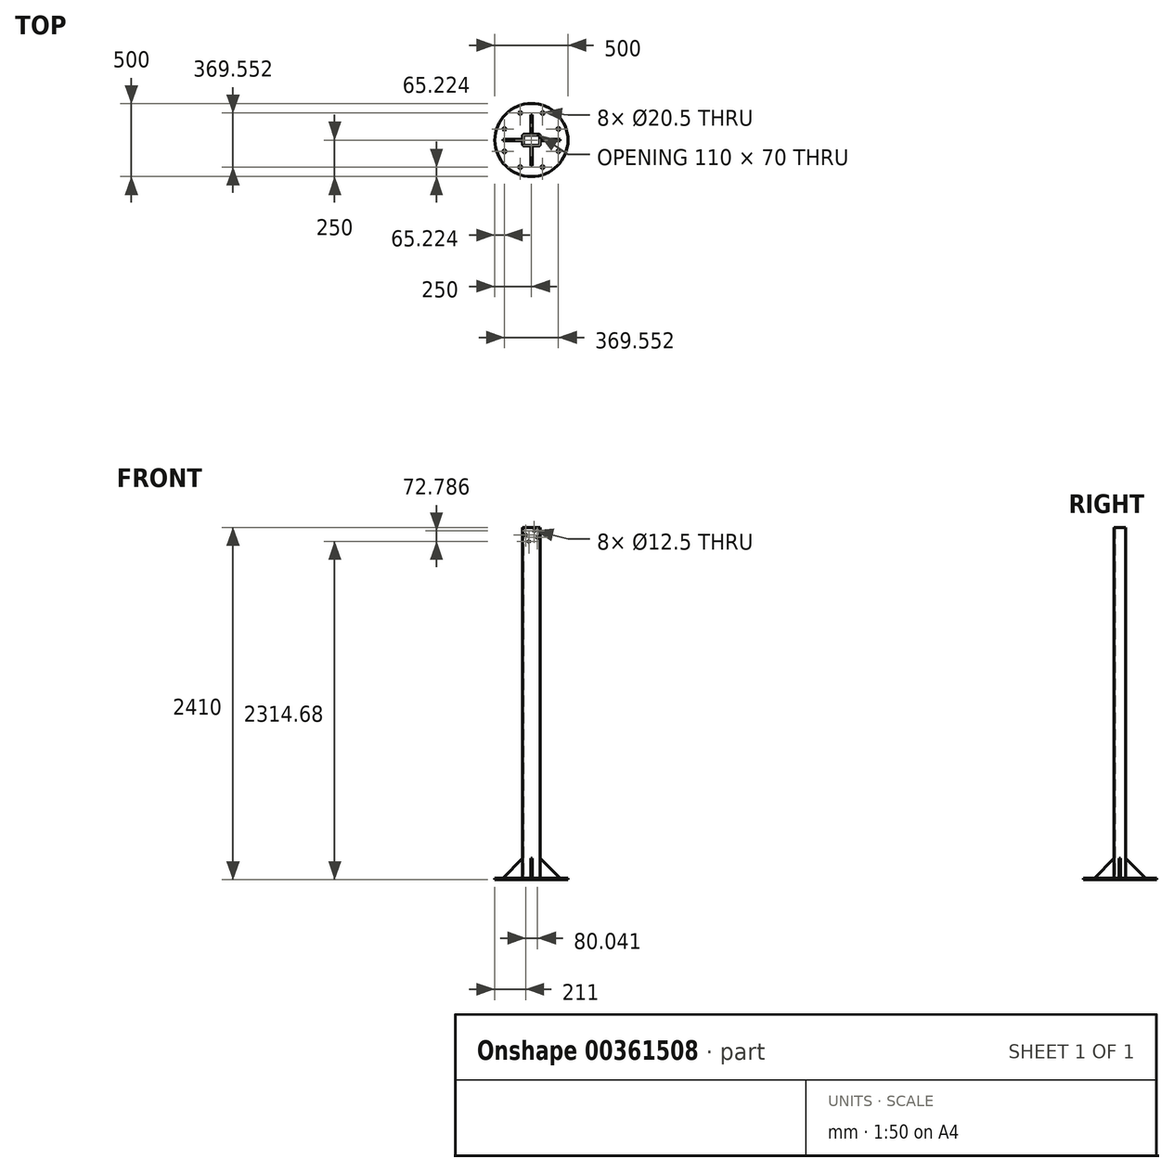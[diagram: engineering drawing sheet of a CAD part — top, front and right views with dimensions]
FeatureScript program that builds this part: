
annotation { "Feature Type Name" : "Feature", "Feature Type Description" : "" }
export const myFeature = defineFeature(function(context is Context, id is Id, definition is map)
    precondition{}
    {
        {
            var Q0;
            Q0=qCreatedBy(makeId("Top.planeOp"),FACE);
            var sketch = newSketch(context, id + "F0", { "sketchPlane" : qUnion([Q0])});
            skCircle(sketch, "E0", {"center": v(0, 0) * mm, "radius": 250 * mm});
            skCircle(sketch, "E1", {"center": v(76.54, 184.78) * mm, "radius": 10.25 * mm});
            skLineSegment(sketch, "E2", {"start": v(0, 0) * mm, "end": v(76.54, 184.78) * mm, "construction": true});
            skCircle(sketch, "E3.1.0", {"center": v(-76.54, 184.78) * mm, "radius": 10.25 * mm});
            skCircle(sketch, "E3.2.0", {"center": v(-184.78, 76.54) * mm, "radius": 10.25 * mm});
            skCircle(sketch, "E3.3.0", {"center": v(-184.78, -76.54) * mm, "radius": 10.25 * mm});
            skLineSegment(sketch, "E4", {"start": v(-76.54, 184.78) * mm, "end": v(0, 0) * mm, "construction": true});
            skCircle(sketch, "E5.1.4.0", {"center": v(-76.54, -184.78) * mm, "radius": 10.25 * mm});
            skCircle(sketch, "E5.1.5.0", {"center": v(76.54, -184.78) * mm, "radius": 10.25 * mm});
            skCircle(sketch, "E5.1.6.0", {"center": v(184.78, -76.54) * mm, "radius": 10.25 * mm});
            skCircle(sketch, "E5.1.7.0", {"center": v(184.78, 76.54) * mm, "radius": 10.25 * mm});
            skSolve(sketch);
        }
        {
            var Q0;
            Q0 = qSketchRegion(id + "F0", true);
            extrude(context, id + "F1", {"entities" : qUnion([Q0]), "depth" : 10 * mm});
        }
        {
            var Q0;
            Q0=makeQuery(id+"F1.opExtrude","CAP_FACE",FACE,{"disambiguationData":[OSD([sQuery(id+"F0.wireOp",EDGE,"E0")])],"isStart":false});
            var sketch = newSketch(context, id + "F2", { "sketchPlane" : qUnion([Q0])});
            skLineSegment(sketch, "E6.bottom", {"start": v(50, 40) * mm, "end": v(-50, 40) * mm});
            skLineSegment(sketch, "E6.top", {"start": v(50, -40) * mm, "end": v(-50, -40) * mm});
            skLineSegment(sketch, "E6.left", {"start": v(60, 30) * mm, "end": v(60, -30) * mm});
            skLineSegment(sketch, "E6.right", {"start": v(-60, 30) * mm, "end": v(-60, -30) * mm});
            skPoint(sketch, "E6.middle", {"position": v(0, 0) * mm});
            skPoint(sketch, "E7.visualSharp", {"position": v(60, 40) * mm});
            skArc(sketch, "E7.filletArc", {"start": v(60, 30) * mm, "mid": v(57.07, 37.07) * mm, "end": v(50, 40) * mm});
            skPoint(sketch, "E8.visualSharp", {"position": v(-60, 40) * mm});
            skArc(sketch, "E8.filletArc", {"start": v(-50, 40) * mm, "mid": v(-57.07, 37.07) * mm, "end": v(-60, 30) * mm});
            skPoint(sketch, "E9.visualSharp", {"position": v(-60, -40) * mm});
            skArc(sketch, "E9.filletArc", {"start": v(-60, -30) * mm, "mid": v(-57.07, -37.07) * mm, "end": v(-50, -40) * mm});
            skPoint(sketch, "E10.visualSharp", {"position": v(60, -40) * mm});
            skArc(sketch, "E10.filletArc", {"start": v(50, -40) * mm, "mid": v(57.07, -37.07) * mm, "end": v(60, -30) * mm});
            skArc(sketch, "E11.0", {"start": v(55, 30) * mm, "mid": v(53.54, 33.54) * mm, "end": v(50, 35) * mm});
            skLineSegment(sketch, "E11.1", {"start": v(55, 30) * mm, "end": v(55, -30) * mm});
            skLineSegment(sketch, "E11.2", {"start": v(50, 35) * mm, "end": v(-50, 35) * mm});
            skArc(sketch, "E11.3", {"start": v(50, -35) * mm, "mid": v(53.54, -33.54) * mm, "end": v(55, -30) * mm});
            skArc(sketch, "E11.4", {"start": v(-50, 35) * mm, "mid": v(-53.54, 33.54) * mm, "end": v(-55, 30) * mm});
            skLineSegment(sketch, "E11.5", {"start": v(-55, 30) * mm, "end": v(-55, -30) * mm});
            skArc(sketch, "E11.6", {"start": v(-55, -30) * mm, "mid": v(-53.54, -33.54) * mm, "end": v(-50, -35) * mm});
            skLineSegment(sketch, "E11.7", {"start": v(50, -35) * mm, "end": v(-50, -35) * mm});
            skSolve(sketch);
        }
        {
            var Q0;
            Q0 = qSketchRegion(id + "F2", true);
            extrude(context, id + "F3", {"entities" : qUnion([Q0]), "depth" : 2400 * mm});
        }
        {
            var Q0;
            Q0=qCreatedBy(makeId("Front.planeOp"),FACE);
            var sketch = newSketch(context, id + "F4", { "sketchPlane" : qUnion([Q0])});
            skLineSegment(sketch, "E12", {"start": v(-60, 145) * mm, "end": v(-195, 10) * mm});
            skLineSegment(sketch, "E13", {"start": v(-195, 10) * mm, "end": v(-60, 10) * mm});
            skLineSegment(sketch, "E14", {"start": v(-60, 10) * mm, "end": v(-60, 145) * mm});
            skSolve(sketch);
        }
        {
            var Q0;
            Q0 = qSketchRegion(id + "F4", true);
            extrude(context, id + "F5", {"entities" : qUnion([Q0]), "endBound" : BoundingType.SYMMETRIC, "depth" : 10 * mm});
        }
        {
            var Q0;
            Q0=qCreatedBy(makeId("Right.planeOp"),FACE);
            var sketch = newSketch(context, id + "F6", { "sketchPlane" : qUnion([Q0])});
            skLineSegment(sketch, "E15", {"start": v(-40, 10) * mm, "end": v(-40, 145) * mm});
            skLineSegment(sketch, "E16", {"start": v(-40, 145) * mm, "end": v(-175, 10) * mm});
            skLineSegment(sketch, "E17", {"start": v(-175, 10) * mm, "end": v(-40, 10) * mm});
            skSolve(sketch);
        }
        {
            var Q0;
            Q0 = qSketchRegion(id + "F6", true);
            extrude(context, id + "F7", {"entities" : qUnion([Q0]), "endBound" : BoundingType.SYMMETRIC, "depth" : 10 * mm});
        }
        {
            var Q0;
            Q0=makeQuery(id+"F7.opExtrude","SWEPT_BODY",BODY,{"disambiguationData":[OSD([sQuery(id+"F6.wireOp",EDGE,"E15"),sQuery(id+"F6.wireOp",EDGE,"E16"),sQuery(id+"F6.wireOp",EDGE,"E17")])]});
            var Q1;
            Q1=qCreatedBy(makeId("Front.planeOp"),FACE);
            mirror(context, id + "F8", {"entities" : qUnion([Q0]), "mirrorPlane" : qUnion([Q1])});
        }
        {
            var Q0;
            Q0=makeQuery(id+"F5.opExtrude","SWEPT_BODY",BODY,{"disambiguationData":[OSD([sQuery(id+"F4.wireOp",EDGE,"E12"),sQuery(id+"F4.wireOp",EDGE,"E13"),sQuery(id+"F4.wireOp",EDGE,"E14")])]});
            var Q1;
            Q1=qCreatedBy(makeId("Right.planeOp"),FACE);
            mirror(context, id + "F9", {"entities" : qUnion([Q0]), "mirrorPlane" : qUnion([Q1])});
        }
        {
            var Q0;
            Q0=makeQuery(id+"F3.opExtrude","SWEPT_FACE",FACE,{"disambiguationData":[OSD([sQuery(id+"F2.wireOp",EDGE,"E6.top")])]});
            var sketch = newSketch(context, id + "F10", { "sketchPlane" : qUnion([Q0])});
            skLineSegment(sketch, "E18", {"start": v(19.91, 2387.47) * mm, "end": v(-39, 2360) * mm, "construction": true});
            skLineSegment(sketch, "E19", {"start": v(-39, 2360) * mm, "end": v(-17.87, 2314.68) * mm, "construction": true});
            skLineSegment(sketch, "E20", {"start": v(-17.87, 2314.68) * mm, "end": v(41.04, 2342.15) * mm, "construction": true});
            skLineSegment(sketch, "E21", {"start": v(41.04, 2342.15) * mm, "end": v(19.91, 2387.47) * mm, "construction": true});
            skCircle(sketch, "E22", {"center": v(19.91, 2387.47) * mm, "radius": 6.25 * mm});
            skCircle(sketch, "E23", {"center": v(-39, 2360) * mm, "radius": 6.25 * mm});
            skCircle(sketch, "E24", {"center": v(-17.87, 2314.68) * mm, "radius": 6.25 * mm});
            skCircle(sketch, "E25", {"center": v(41.04, 2342.15) * mm, "radius": 6.25 * mm});
            skSolve(sketch);
        }
        {
            var Q0;
            Q0 = qSketchRegion(id + "F10", true);
            extrude(context, id + "F11", {"entities" : qUnion([Q0]), "operationType" : NewBodyOperationType.REMOVE, "endBound" : BoundingType.THROUGH_ALL, "oppositeDirection" : true, "depth" : 25 * mm});
        }
    });
